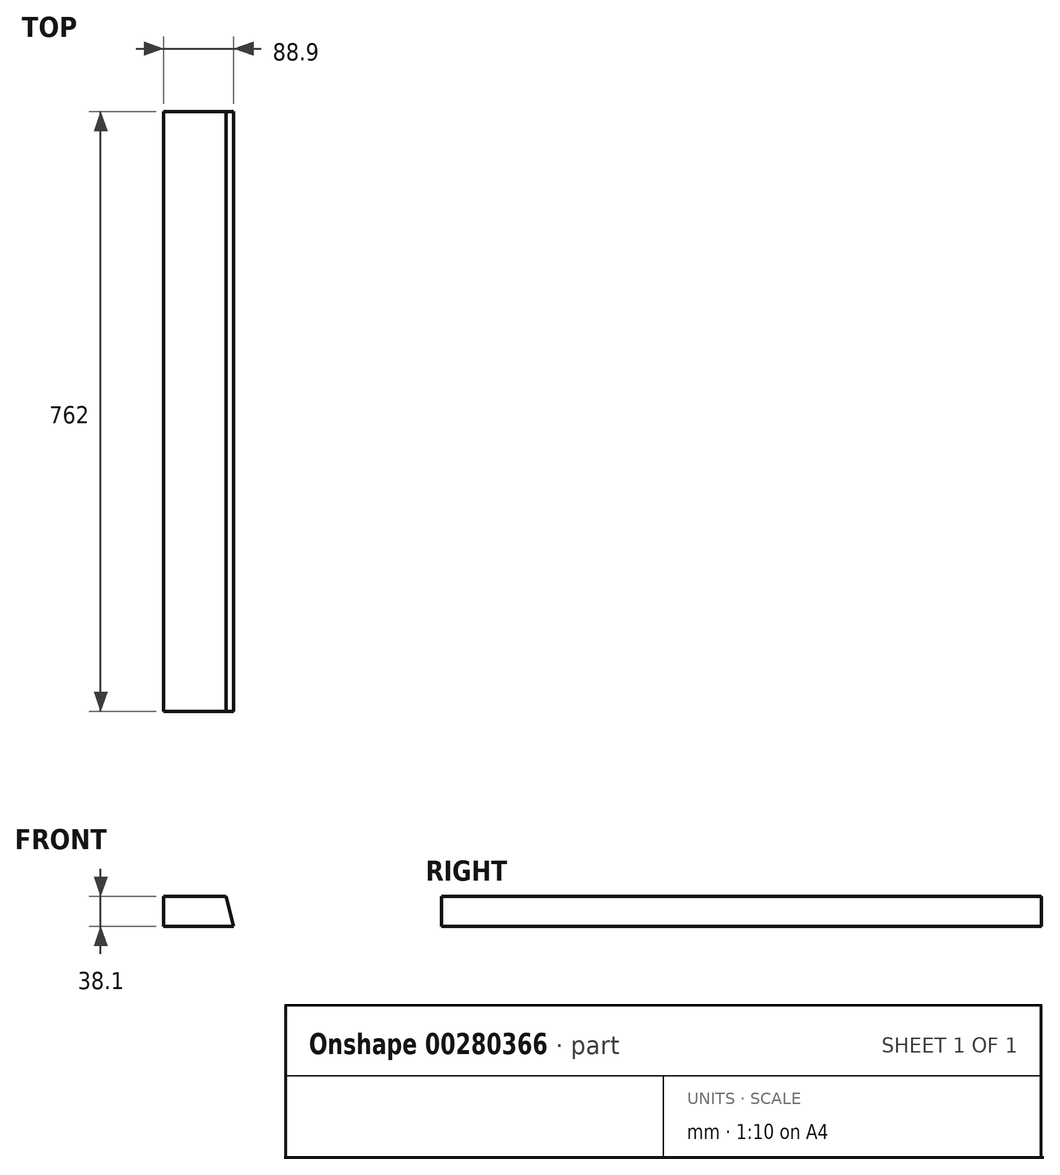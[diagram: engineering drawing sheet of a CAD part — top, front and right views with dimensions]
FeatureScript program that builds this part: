
annotation { "Feature Type Name" : "Feature", "Feature Type Description" : "" }
export const myFeature = defineFeature(function(context is Context, id is Id, definition is map)
    precondition{}
    {
        {
            var Q0;
            Q0=qCreatedBy(makeId("Front.planeOp"),FACE);
            var sketch = newSketch(context, id + "F0", { "sketchPlane" : qUnion([Q0])});
            skLineSegment(sketch, "E0.bottom", {"start": v(-21.28, 2.95) * mm, "end": v(67.62, 2.95) * mm});
            skLineSegment(sketch, "E0.top", {"start": v(-21.28, -35.15) * mm, "end": v(67.62, -35.15) * mm});
            skLineSegment(sketch, "E0.left", {"start": v(-21.28, 2.95) * mm, "end": v(-21.28, -35.15) * mm});
            skLineSegment(sketch, "E0.right", {"start": v(67.62, 2.95) * mm, "end": v(67.62, -35.15) * mm});
            skLineSegment(sketch, "E1", {"start": v(67.62, -35.15) * mm, "end": v(58.04, 2.95) * mm});
            skSolve(sketch);
        }
        {
            var Q0;
            Q0=makeQuery(id+"F0.imprint","IMPRINT",FACE,{"disambiguationData":[TD([[makeQuery(id+"F0.imprint","IMPRINT",EDGE,{"derivedFrom":sQuery(id+"F0.wireOp",EDGE,"E0.top")}),1.0]])]});
            extrude(context, id + "F1", {"entities" : qUnion([Q0]), "oppositeDirection" : true, "depth" : 762 * mm});
        }
    });
